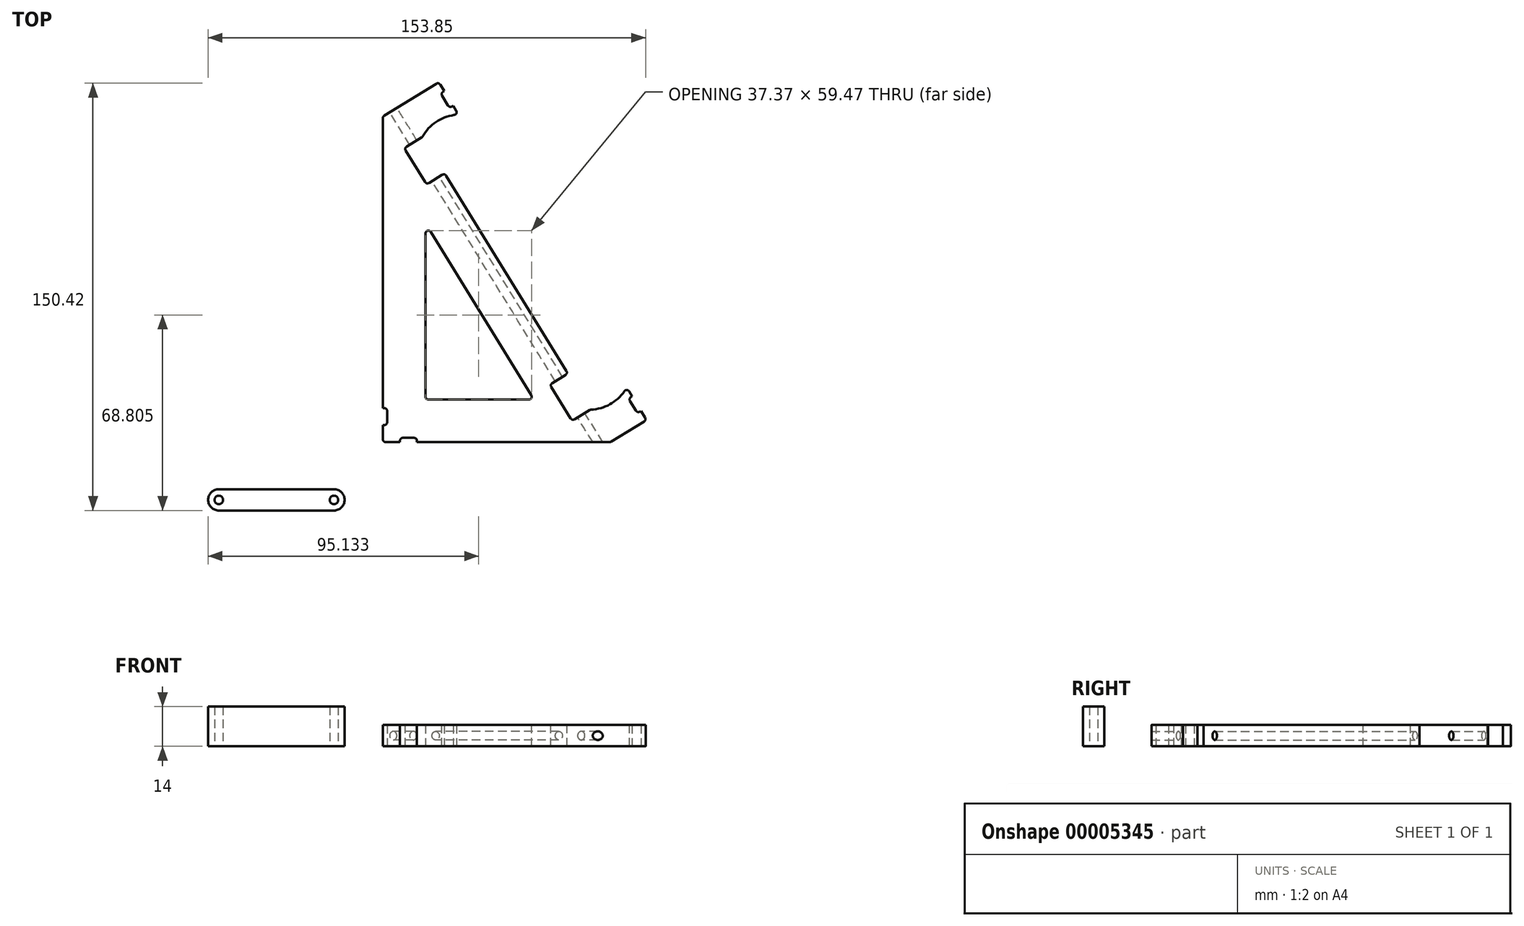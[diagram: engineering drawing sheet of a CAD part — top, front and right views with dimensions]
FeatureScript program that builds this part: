
annotation { "Feature Type Name" : "Feature", "Feature Type Description" : "" }
export const myFeature = defineFeature(function(context is Context, id is Id, definition is map)
    precondition{}
    {
        {
            var Q0;
            Q0=qCreatedBy(makeId("Top.planeOp"),FACE);
            var sketch = newSketch(context, id + "F0", { "sketchPlane" : qUnion([Q0])});
            skLineSegment(sketch, "E0", {"start": v(0, 0) * mm, "end": v(0, 130) * mm, "construction": true});
            skLineSegment(sketch, "E1", {"start": v(0, 130) * mm, "end": v(80, 0) * mm, "construction": true});
            skLineSegment(sketch, "E2", {"start": v(80, 0) * mm, "end": v(0, 0) * mm, "construction": true});
            skLineSegment(sketch, "E3", {"start": v(19.63, 126.73) * mm, "end": v(26.66, 115.3) * mm, "construction": true});
            skLineSegment(sketch, "E4", {"start": v(26.66, 115.3) * mm, "end": v(13.89, 107.43) * mm, "construction": true});
            skLineSegment(sketch, "E5", {"start": v(80, 0) * mm, "end": v(92.77, 7.86) * mm});
            skLineSegment(sketch, "E6", {"start": v(92.77, 7.86) * mm, "end": v(85.74, 19.3) * mm, "construction": true});
            skLineSegment(sketch, "E7", {"start": v(85.74, 19.3) * mm, "end": v(72.97, 11.43) * mm, "construction": true});
            skLineSegment(sketch, "E8", {"start": v(72.97, 11.43) * mm, "end": v(66.58, 7.5) * mm});
            skLineSegment(sketch, "E9", {"start": v(66.58, 7.5) * mm, "end": v(58.72, 20.27) * mm});
            skLineSegment(sketch, "E10", {"start": v(58.72, 20.27) * mm, "end": v(65.1, 24.2) * mm});
            skLineSegment(sketch, "E11", {"start": v(13.89, 107.43) * mm, "end": v(7.5, 103.5) * mm});
            skLineSegment(sketch, "E12", {"start": v(7.5, 103.5) * mm, "end": v(15.36, 90.73) * mm});
            skLineSegment(sketch, "E13", {"start": v(15.36, 90.73) * mm, "end": v(21.75, 94.66) * mm});
            skLineSegment(sketch, "E14", {"start": v(19.63, 126.73) * mm, "end": v(0, 114.65) * mm});
            skLineSegment(sketch, "E15", {"start": v(0, 114.65) * mm, "end": v(0, 12) * mm});
            skLineSegment(sketch, "E16", {"start": v(21.75, 94.66) * mm, "end": v(65.1, 24.2) * mm});
            skArc(sketch, "E17", {"start": v(72.97, 11.43) * mm, "mid": v(80.4, 13.65) * mm, "end": v(85.74, 19.3) * mm});
            skArc(sketch, "E18", {"start": v(26.66, 115.3) * mm, "mid": v(19.22, 113.08) * mm, "end": v(13.89, 107.43) * mm});
            skLineSegment(sketch, "E19", {"start": v(15, 15) * mm, "end": v(15, 77) * mm});
            skLineSegment(sketch, "E20", {"start": v(15, 77) * mm, "end": v(53.16, 15) * mm});
            skLineSegment(sketch, "E21", {"start": v(53.16, 15) * mm, "end": v(15, 15) * mm});
            skLineSegment(sketch, "E22", {"start": v(6, 0) * mm, "end": v(6, 1.5) * mm});
            skLineSegment(sketch, "E23", {"start": v(6, 1.5) * mm, "end": v(12, 1.5) * mm});
            skLineSegment(sketch, "E24", {"start": v(12, 1.5) * mm, "end": v(12, 0) * mm});
            skLineSegment(sketch, "E25", {"start": v(0, 6) * mm, "end": v(1.5, 6) * mm});
            skLineSegment(sketch, "E26", {"start": v(1.5, 6) * mm, "end": v(1.5, 12) * mm});
            skLineSegment(sketch, "E27", {"start": v(1.5, 12) * mm, "end": v(0, 12) * mm});
            skLineSegment(sketch, "E28.trimOffspring", {"start": v(0, 6) * mm, "end": v(0, 0) * mm});
            skLineSegment(sketch, "E29", {"start": v(0, 0) * mm, "end": v(6, 0) * mm});
            skLineSegment(sketch, "E30", {"start": v(12, 0) * mm, "end": v(80, 0) * mm});
            skLineSegment(sketch, "E31", {"start": v(21.57, 123.56) * mm, "end": v(20.3, 122.78) * mm});
            skLineSegment(sketch, "E32", {"start": v(20.3, 122.78) * mm, "end": v(23.44, 117.67) * mm});
            skLineSegment(sketch, "E33", {"start": v(23.44, 117.67) * mm, "end": v(24.72, 118.45) * mm});
            skLineSegment(sketch, "E34", {"start": v(19.63, 126.73) * mm, "end": v(21.57, 123.56) * mm});
            skLineSegment(sketch, "E35", {"start": v(24.72, 118.45) * mm, "end": v(26.66, 115.3) * mm});
            skLineSegment(sketch, "E36", {"start": v(85.74, 19.3) * mm, "end": v(87.69, 16.13) * mm});
            skLineSegment(sketch, "E37", {"start": v(87.69, 16.13) * mm, "end": v(86.4, 15.35) * mm});
            skLineSegment(sketch, "E38", {"start": v(86.4, 15.35) * mm, "end": v(89.55, 10.24) * mm});
            skLineSegment(sketch, "E39", {"start": v(89.55, 10.24) * mm, "end": v(90.83, 11.02) * mm});
            skLineSegment(sketch, "E40", {"start": v(90.83, 11.02) * mm, "end": v(92.77, 7.86) * mm});
            skSolve(sketch);
        }
        {
            var Q0;
            Q0=makeQuery(id+"F0.imprint","IMPRINT",FACE,{"disambiguationData":[TD([[makeQuery(id+"F0.imprint","IMPRINT",EDGE,{"derivedFrom":sQuery(id+"F0.wireOp",EDGE,"E5")}),1.0]])]});
            extrude(context, id + "F1", {"entities" : qUnion([Q0]), "depth" : 7.5 * mm});
        }
        {
            var Q0;
            Q0=qCreatedBy(makeId("Top.planeOp"),FACE);
            var sketch = newSketch(context, id + "F2", { "sketchPlane" : qUnion([Q0])});
            skLineSegment(sketch, "E41", {"start": v(-57.7, -16.57) * mm, "end": v(-17.2, -16.57) * mm});
            skLineSegment(sketch, "E42", {"start": v(-17.2, -24.07) * mm, "end": v(-57.7, -24.07) * mm});
            skArc(sketch, "E43", {"start": v(-57.7, -24.07) * mm, "mid": v(-61.45, -20.32) * mm, "end": v(-57.7, -16.57) * mm});
            skArc(sketch, "E44", {"start": v(-17.2, -24.07) * mm, "mid": v(-13.45, -20.32) * mm, "end": v(-17.2, -16.57) * mm});
            skCircle(sketch, "E45", {"center": v(-57.7, -20.32) * mm, "radius": 1.5 * mm});
            skCircle(sketch, "E46", {"center": v(-17.2, -20.32) * mm, "radius": 1.5 * mm});
            skSolve(sketch);
        }
        {
            var Q0;
            Q0=makeQuery(id+"F2.imprint","IMPRINT",FACE,{"disambiguationData":[TD([[makeQuery(id+"F2.imprint","IMPRINT",EDGE,{"derivedFrom":sQuery(id+"F2.wireOp",EDGE,"E41")}),-1.0]])]});
            extrude(context, id + "F3", {"entities" : qUnion([Q0]), "depth" : 14 * mm});
        }
        {
            var Q0;
            Q0=makeQuery(id+"F1.opExtrude","SWEPT_FACE",FACE,{"disambiguationData":[OSD([sQuery(id+"F0.wireOp",EDGE,"E13")])]});
            var sketch = newSketch(context, id + "F4", { "sketchPlane" : qUnion([Q0])});
            skLineSegment(sketch, "E47", {"start": v(-60.63, 0) * mm, "end": v(-68.13, 7.5) * mm, "construction": true});
            skLineSegment(sketch, "E48", {"start": v(-60.63, 7.5) * mm, "end": v(-68.13, 0) * mm, "construction": true});
            skCircle(sketch, "E49", {"center": v(-64.38, 3.75) * mm, "radius": 1.5 * mm});
            skSolve(sketch);
        }
        {
            var Q0;
            Q0=makeQuery(id+"F4.imprint","IMPRINT",FACE,{"disambiguationData":[TD([[makeQuery(id+"F4.imprint","IMPRINT",EDGE,{"derivedFrom":sQuery(id+"F4.wireOp",EDGE,"E49")}),1.0]])]});
            extrude(context, id + "F5", {"entities" : qUnion([Q0]), "operationType" : NewBodyOperationType.REMOVE, "endBound" : BoundingType.SYMMETRIC, "oppositeDirection" : true, "depth" : 500 * mm});
        }
        {
            var Q0;
            Q0=makeQuery(id+"F1.opExtrude","SWEPT_EDGE",EDGE,{"disambiguationData":[OSD([sQuery(id+"F0.wireOp",EDGE,"E3"),sQuery(id+"F0.wireOp",EDGE,"E14")])]});
            var Q1;
            Q1=makeQuery(id+"F1.opExtrude","SWEPT_EDGE",EDGE,{"disambiguationData":[OSD([sQuery(id+"F0.wireOp",EDGE,"E14"),sQuery(id+"F0.wireOp",EDGE,"E15")])]});
            var Q2;
            Q2=makeQuery(id+"F1.opExtrude","SWEPT_EDGE",EDGE,{"disambiguationData":[OSD([sQuery(id+"F0.wireOp",EDGE,"E3"),sQuery(id+"F0.wireOp",EDGE,"E18")])]});
            var Q3;
            Q3=makeQuery(id+"F1.opExtrude","SWEPT_EDGE",EDGE,{"disambiguationData":[OSD([sQuery(id+"F0.wireOp",EDGE,"E12"),sQuery(id+"F0.wireOp",EDGE,"E13")])]});
            var Q4;
            Q4=makeQuery(id+"F1.opExtrude","SWEPT_EDGE",EDGE,{"disambiguationData":[OSD([sQuery(id+"F0.wireOp",EDGE,"E13"),sQuery(id+"F0.wireOp",EDGE,"E16")])]});
            var Q5;
            Q5=makeQuery(id+"F1.opExtrude","SWEPT_EDGE",EDGE,{"disambiguationData":[OSD([sQuery(id+"F0.wireOp",EDGE,"E11"),sQuery(id+"F0.wireOp",EDGE,"E12")])]});
            var Q6;
            Q6=makeQuery(id+"F1.opExtrude","SWEPT_EDGE",EDGE,{"disambiguationData":[OSD([sQuery(id+"F0.wireOp",EDGE,"E11"),sQuery(id+"F0.wireOp",EDGE,"E18")])]});
            var Q7;
            Q7=makeQuery(id+"F1.opExtrude","SWEPT_EDGE",EDGE,{"disambiguationData":[OSD([sQuery(id+"F0.wireOp",EDGE,"E19"),sQuery(id+"F0.wireOp",EDGE,"E20")])]});
            var Q8;
            Q8=makeQuery(id+"F1.opExtrude","SWEPT_EDGE",EDGE,{"disambiguationData":[OSD([sQuery(id+"F0.wireOp",EDGE,"E10"),sQuery(id+"F0.wireOp",EDGE,"E16")])]});
            var Q9;
            Q9=makeQuery(id+"F1.opExtrude","SWEPT_EDGE",EDGE,{"disambiguationData":[OSD([sQuery(id+"F0.wireOp",EDGE,"E5"),sQuery(id+"F0.wireOp",EDGE,"E6")])]});
            var Q10;
            Q10=makeQuery(id+"F1.opExtrude","SWEPT_EDGE",EDGE,{"disambiguationData":[OSD([sQuery(id+"F0.wireOp",EDGE,"E5"),sQuery(id+"F0.wireOp",EDGE,"E30")])]});
            var Q11;
            Q11=makeQuery(id+"F1.opExtrude","SWEPT_EDGE",EDGE,{"disambiguationData":[OSD([sQuery(id+"F0.wireOp",EDGE,"E22"),sQuery(id+"F0.wireOp",EDGE,"E23")])]});
            var Q12;
            Q12=makeQuery(id+"F1.opExtrude","SWEPT_EDGE",EDGE,{"disambiguationData":[OSD([sQuery(id+"F0.wireOp",EDGE,"E28.trimOffspring"),sQuery(id+"F0.wireOp",EDGE,"E29")])]});
            var Q13;
            Q13=makeQuery(id+"F1.opExtrude","SWEPT_EDGE",EDGE,{"disambiguationData":[OSD([sQuery(id+"F0.wireOp",EDGE,"E23"),sQuery(id+"F0.wireOp",EDGE,"E24")])]});
            var Q14;
            Q14=makeQuery(id+"F1.opExtrude","SWEPT_EDGE",EDGE,{"disambiguationData":[OSD([sQuery(id+"F0.wireOp",EDGE,"E26"),sQuery(id+"F0.wireOp",EDGE,"E27")])]});
            var Q15;
            Q15=makeQuery(id+"F1.opExtrude","SWEPT_EDGE",EDGE,{"disambiguationData":[OSD([sQuery(id+"F0.wireOp",EDGE,"E25"),sQuery(id+"F0.wireOp",EDGE,"E26")])]});
            var Q16;
            Q16=makeQuery(id+"F1.opExtrude","SWEPT_EDGE",EDGE,{"disambiguationData":[OSD([sQuery(id+"F0.wireOp",EDGE,"E20"),sQuery(id+"F0.wireOp",EDGE,"E21")])]});
            var Q17;
            Q17=makeQuery(id+"F1.opExtrude","SWEPT_EDGE",EDGE,{"disambiguationData":[OSD([sQuery(id+"F0.wireOp",EDGE,"E19"),sQuery(id+"F0.wireOp",EDGE,"E21")])]});
            var Q18;
            Q18=makeQuery(id+"F1.opExtrude","SWEPT_EDGE",EDGE,{"disambiguationData":[OSD([sQuery(id+"F0.wireOp",EDGE,"E6"),sQuery(id+"F0.wireOp",EDGE,"E17")])]});
            var Q19;
            Q19=makeQuery(id+"F1.opExtrude","SWEPT_EDGE",EDGE,{"disambiguationData":[OSD([sQuery(id+"F0.wireOp",EDGE,"E8"),sQuery(id+"F0.wireOp",EDGE,"E17")])]});
            var Q20;
            Q20=makeQuery(id+"F1.opExtrude","SWEPT_EDGE",EDGE,{"disambiguationData":[OSD([sQuery(id+"F0.wireOp",EDGE,"E8"),sQuery(id+"F0.wireOp",EDGE,"E9")])]});
            var Q21;
            Q21=makeQuery(id+"F1.opExtrude","SWEPT_EDGE",EDGE,{"disambiguationData":[OSD([sQuery(id+"F0.wireOp",EDGE,"E9"),sQuery(id+"F0.wireOp",EDGE,"E10")])]});
            var Q22;
            Q22=makeQuery(id+"F1.opExtrude","SWEPT_EDGE",EDGE,{"disambiguationData":[OSD([sQuery(id+"F0.wireOp",EDGE,"E31"),sQuery(id+"F0.wireOp",EDGE,"E32")])]});
            var Q23;
            Q23=makeQuery(id+"F1.opExtrude","SWEPT_EDGE",EDGE,{"disambiguationData":[OSD([sQuery(id+"F0.wireOp",EDGE,"E32"),sQuery(id+"F0.wireOp",EDGE,"E33")])]});
            var Q24;
            Q24=makeQuery(id+"F1.opExtrude","SWEPT_EDGE",EDGE,{"disambiguationData":[OSD([sQuery(id+"F0.wireOp",EDGE,"E38"),sQuery(id+"F0.wireOp",EDGE,"E39")])]});
            var Q25;
            Q25=makeQuery(id+"F1.opExtrude","SWEPT_EDGE",EDGE,{"disambiguationData":[OSD([sQuery(id+"F0.wireOp",EDGE,"E37"),sQuery(id+"F0.wireOp",EDGE,"E38")])]});
            fillet(context, id + "F6", {"entities" : qUnion([Q0, Q1, Q2, Q3, Q4, Q5, Q6, Q7, Q8, Q9, Q10, Q11, Q12, Q13, Q14, Q15, Q16, Q17, Q18, Q19, Q20, Q21, Q22, Q23, Q24, Q25]), "radius" : 1 * mm, "tangentPropagation" : true, "allowEdgeOverflow" : false});
        }
    });
